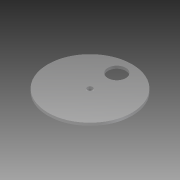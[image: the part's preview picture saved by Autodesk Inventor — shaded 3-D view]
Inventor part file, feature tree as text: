
AUTODESK INVENTOR PART (.ipt)
format: ipt  version: 2015 (Build 190159000, 159)  size: 79,360 bytes
history: native  units: mm
features: extrude x1, sketch x1
ambient origin geometry x8: Origin, YZ Plane, XZ Plane, XY Plane, X Axis, Y Axis, Z Axis, Center Point
bodies: Body1 (feature_tree)
feature tree (2):
  extrude  "Extrusion2"  Depth=3.0mm
  sketch  "Sketch1"  dims[d0=94.0mm d1=5.9mm d4=20.0mm d5=30.0mm d6=3.0mm d7=0.0mm]
